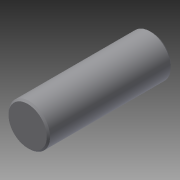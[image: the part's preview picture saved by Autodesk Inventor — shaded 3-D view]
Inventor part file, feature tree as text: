
AUTODESK INVENTOR PART (.ipt)
format: ipt  version: 2014 SP2 (Build 180246200, 246)  size: 100,864 bytes
history: native  units: in
note: dims shown in document units (in); Inventor stores cm internally (conversion verified against a paired STEP export)
features: other x35, revolve x1, sketch x1
ambient origin geometry x8: Origin, YZ Plane, XZ Plane, XY Plane, X Axis, Y Axis, Z Axis, Center Point
bodies: Solid1 (feature_tree)
feature tree (37):
  revolve  "Revolution1"  [1 undecoded]
  other  "dia1_XY"
  other  "dia1_YZ"
  other  "dia1_ZX"
  other  "dia1_X"
  other  "dia1_Y"
  other  "dia1_Z"
  other  "dia1_Center"
  other  "dia2_XY"
  other  "dia2_YZ"
  other  "dia2_ZX"
  other  "dia2_X"
  other  "dia2_Y"
  other  "dia2_Z"
  other  "dia2_Center"
  other  "pin_XY"
  other  "pin_YZ"
  other  "pin_ZX"
  other  "pin_X"
  other  "pin_Y"
  other  "pin_Z"
  other  "pin_Center"
  other  "pin1_XY"
  other  "pin1_YZ"
  other  "pin1_ZX"
  other  "pin1_X"
  other  "pin1_Y"
  other  "pin1_Z"
  other  "pin1_Center"
  other  "pin2_XY"
  other  "pin2_YZ"
  other  "pin2_ZX"
  other  "pin2_X"
  other  "pin2_Y"
  other  "pin2_Z"
  other  "pin2_Center"
  sketch  "Sketch_1"  dims[d0=360.0deg]
note: 1 required parameter value undecoded (feature->parameter linkage not recoverable at this tier; creation-order binding heuristic only, values carry confidence <= 0.55)
